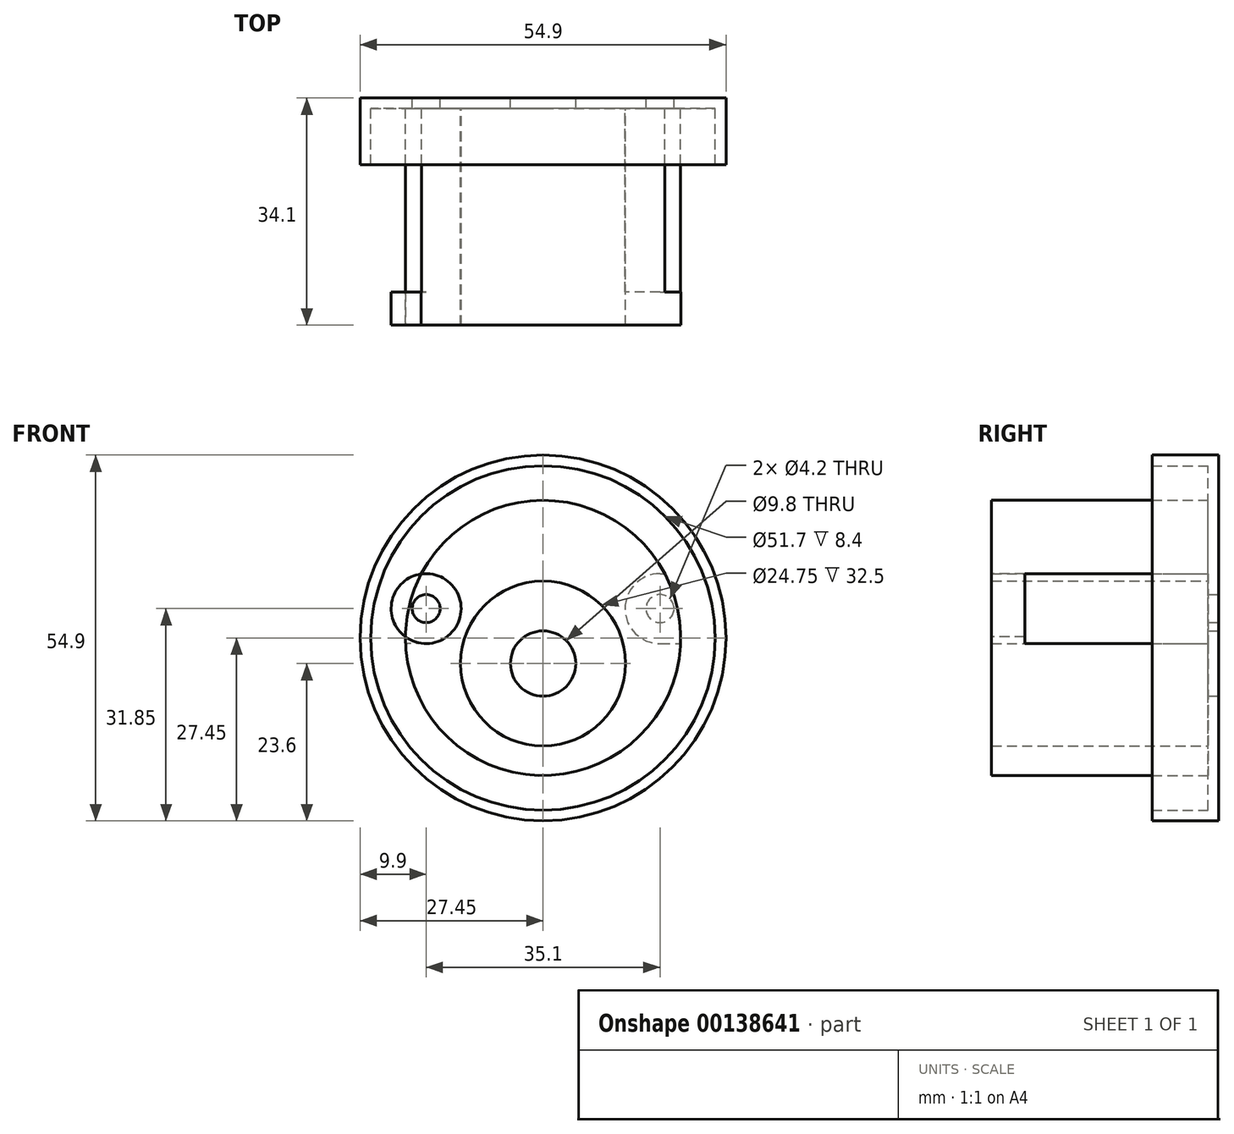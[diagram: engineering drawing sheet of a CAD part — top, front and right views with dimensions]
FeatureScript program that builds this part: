
annotation { "Feature Type Name" : "Feature", "Feature Type Description" : "" }
export const myFeature = defineFeature(function(context is Context, id is Id, definition is map)
    precondition{}
    {
        {
            var Q0;
            Q0=qCreatedBy(makeId("Front.planeOp"),FACE);
            var sketch = newSketch(context, id + "F0", { "sketchPlane" : qUnion([Q0])});
            skCircle(sketch, "E0", {"center": v(0, 0) * mm, "radius": 25.85 * mm});
            skCircle(sketch, "E1.0", {"center": v(0, 0) * mm, "radius": 27.45 * mm});
            skCircle(sketch, "E2", {"center": v(0, -3.85) * mm, "radius": 4.9 * mm});
            skCircle(sketch, "E3", {"center": v(-17.55, 4.4) * mm, "radius": 2.1 * mm});
            skCircle(sketch, "E4", {"center": v(17.55, 4.4) * mm, "radius": 2.1 * mm});
            skLineSegment(sketch, "E5", {"start": v(-17.55, 2.3) * mm, "end": v(17.55, 2.3) * mm, "construction": true});
            skPoint(sketch, "E6", {"position": v(0, 2.3) * mm});
            skCircle(sketch, "E7", {"center": v(0, -3.85) * mm, "radius": 12 * mm, "construction": true});
            skSolve(sketch);
        }
        {
            var Q0;
            Q0=makeQuery(id+"F0.imprint","IMPRINT",FACE,{"disambiguationData":[TD([[makeQuery(id+"F0.imprint","IMPRINT",EDGE,{"derivedFrom":sQuery(id+"F0.wireOp",EDGE,"E0")}),1.0]])]});
            var Q1;
            Q1=makeQuery(id+"F0.imprint","IMPRINT",FACE,{"disambiguationData":[TD([[makeQuery(id+"F0.imprint","IMPRINT",EDGE,{"derivedFrom":sQuery(id+"F0.wireOp",EDGE,"E3")}),-1.0]])]});
            var Q2;
            Q2=makeQuery(id+"F0.imprint","IMPRINT",FACE,{"disambiguationData":[TD([[makeQuery(id+"F0.imprint","IMPRINT",EDGE,{"derivedFrom":sQuery(id+"F0.wireOp",EDGE,"E2")}),-1.0]])]});
            extrude(context, id + "F1", {"entities" : qUnion([Q0, Q1, Q2]), "depth" : 1.6 * mm});
        }
        {
            var Q0;
            Q0=makeQuery(id+"F0.imprint","IMPRINT",FACE,{"disambiguationData":[TD([[makeQuery(id+"F0.imprint","IMPRINT",EDGE,{"derivedFrom":sQuery(id+"F0.wireOp",EDGE,"E0")}),-1.0]])]});
            extrude(context, id + "F2", {"entities" : qUnion([Q0]), "operationType" : NewBodyOperationType.ADD, "depth" : 10 * mm});
        }
        {
            var Q0;
            Q0=makeQuery(id+"F1.opExtrude","CAP_FACE",FACE,{"disambiguationData":[OSD([sQuery(id+"F0.wireOp",EDGE,"E0"),sQuery(id+"F0.wireOp",EDGE,"E2"),sQuery(id+"F0.wireOp",EDGE,"E3"),sQuery(id+"F0.wireOp",EDGE,"E4"),sQuery(id+"F0.wireOp",EDGE,"PUMCyOhg-vD6y-72TI-7Vvg-jFPLf84NLlKd"),sQuery(id+"F0.wireOp",EDGE,"dd9b8376-963c-4b41-b7ff-f7739df00472.0")])],"isStart":false});
            var sketch = newSketch(context, id + "F3", { "sketchPlane" : qUnion([Q0])});
            skCircle(sketch, "E8", {"center": v(0, -3.85) * mm, "radius": 12.38 * mm});
            skCircle(sketch, "E9.0", {"center": v(0, 0) * mm, "radius": 20.65 * mm});
            skCircle(sketch, "E10", {"center": v(-17.55, 4.4) * mm, "radius": 5.25 * mm});
            skCircle(sketch, "E11", {"center": v(17.55, 4.4) * mm, "radius": 5.25 * mm});
            skLineSegment(sketch, "E12", {"start": v(-17.55, 9.65) * mm, "end": v(-18.26, 9.65) * mm});
            skLineSegment(sketch, "E13", {"start": v(-17.55, -0.85) * mm, "end": v(-20.63, -0.85) * mm});
            skLineSegment(sketch, "E14", {"start": v(17.55, 9.65) * mm, "end": v(18.26, 9.65) * mm});
            skLineSegment(sketch, "E15", {"start": v(17.55, -0.85) * mm, "end": v(20.63, -0.85) * mm});
            skSolve(sketch);
        }
        {
            var Q0;
            {var subQ1=sQuery(id+"F3.wireOp",EDGE,"E9.0");var subQ5=sQuery(id+"F3.wireOp",EDGE,"E8");var subQ8=makeQuery(id+"F3.imprint","INTERSECT",VERTEX,{"disambiguationData":[OD(0.0)],"derivedFrom":[subQ5,subQ1]});Q0=makeQuery(id+"F3.imprint","IMPRINT",FACE,{"disambiguationData":[TD([[makeQuery(id+"F3.imprint","IMPRINT",EDGE,{"disambiguationData":[TD([[subQ8,-1.0]])],"derivedFrom":subQ5}),-1.0]])]});}
            extrude(context, id + "F4", {"entities" : qUnion([Q0]), "operationType" : NewBodyOperationType.ADD, "depth" : 32.5 * mm});
        }
        {
            var Q0;
            Q0=makeQuery(id+"F4.opExtrude","CAP_FACE",FACE,{"disambiguationData":[OSD([sQuery(id+"F3.wireOp",EDGE,"E8"),sQuery(id+"F3.wireOp",EDGE,"E9.0"),sQuery(id+"F3.wireOp",EDGE,"E10"),sQuery(id+"F3.wireOp",EDGE,"E11")])],"isStart":false});
            var sketch = newSketch(context, id + "F5", { "sketchPlane" : qUnion([Q0])});
            skCircle(sketch, "E16", {"center": v(-17.55, 4.4) * mm, "radius": 5.25 * mm});
            skCircle(sketch, "E17", {"center": v(17.55, 4.4) * mm, "radius": 5.25 * mm});
            skCircle(sketch, "E18", {"center": v(0, 0) * mm, "radius": 20.65 * mm});
            skLineSegment(sketch, "E19", {"start": v(-17.55, -0.85) * mm, "end": v(-20.63, -0.85) * mm});
            skLineSegment(sketch, "E20", {"start": v(-20.63, -0.85) * mm, "end": v(-20.67, 0.18) * mm});
            skLineSegment(sketch, "E21", {"start": v(-17.55, 9.65) * mm, "end": v(-18.26, 9.65) * mm});
            skLineSegment(sketch, "E22", {"start": v(-18.26, 9.65) * mm, "end": v(-18.28, 9.6) * mm});
            skLineSegment(sketch, "E23", {"start": v(17.55, 9.65) * mm, "end": v(18.26, 9.65) * mm});
            skLineSegment(sketch, "E24", {"start": v(18.26, 9.65) * mm, "end": v(18.28, 9.6) * mm});
            skLineSegment(sketch, "E25", {"start": v(17.55, -0.85) * mm, "end": v(20.63, -0.85) * mm});
            skLineSegment(sketch, "E26", {"start": v(20.63, -0.85) * mm, "end": v(20.67, 0.18) * mm});
            skSolve(sketch);
        }
        {
            var Q0;
            {var subQ0=sQuery(id+"F5.wireOp",EDGE,"E18");var subQ1=sQuery(id+"F5.wireOp",EDGE,"E16");var subQ2=makeQuery(id+"F5.imprint","INTERSECT",VERTEX,{"disambiguationData":[OD(0.0)],"derivedFrom":[subQ1,subQ0]});Q0=makeQuery(id+"F5.imprint","IMPRINT",FACE,{"disambiguationData":[TD([[makeQuery(id+"F5.imprint","IMPRINT",EDGE,{"disambiguationData":[TD([[subQ2,1.0]])],"derivedFrom":subQ1}),1.0]])]});}
            var Q1;
            {var subQ0=sQuery(id+"F5.wireOp",EDGE,"E21");Q1=makeQuery(id+"F5.imprint","IMPRINT",FACE,{"disambiguationData":[TD([[makeQuery(id+"F5.imprint","IMPRINT",EDGE,{"derivedFrom":subQ0}),1.0]])]});}
            var Q2;
            {var subQ0=sQuery(id+"F5.wireOp",EDGE,"E19");Q2=makeQuery(id+"F5.imprint","IMPRINT",FACE,{"disambiguationData":[TD([[makeQuery(id+"F5.imprint","IMPRINT",EDGE,{"derivedFrom":subQ0}),-1.0]])]});}
            var Q3;
            {var subQ0=sQuery(id+"F5.wireOp",EDGE,"E17");var subQ1=makeQuery(id+"F5.imprint","INTERSECT",VERTEX,{"derivedFrom":[subQ0,sQuery(id+"F5.wireOp",EDGE,"E23")]});Q3=makeQuery(id+"F5.imprint","IMPRINT",FACE,{"disambiguationData":[TD([[makeQuery(id+"F5.imprint","IMPRINT",EDGE,{"disambiguationData":[TD([[subQ1,1.0]])],"derivedFrom":subQ0}),1.0]])]});}
            var Q4;
            {var subQ0=sQuery(id+"F5.wireOp",EDGE,"E25");Q4=makeQuery(id+"F5.imprint","IMPRINT",FACE,{"disambiguationData":[TD([[makeQuery(id+"F5.imprint","IMPRINT",EDGE,{"derivedFrom":subQ0}),1.0]])]});}
            var Q5;
            {var subQ0=sQuery(id+"F5.wireOp",EDGE,"E23");Q5=makeQuery(id+"F5.imprint","IMPRINT",FACE,{"disambiguationData":[TD([[makeQuery(id+"F5.imprint","IMPRINT",EDGE,{"derivedFrom":subQ0}),-1.0]])]});}
            extrude(context, id + "F6", {"entities" : qUnion([Q0, Q1, Q2, Q3, Q4, Q5]), "operationType" : NewBodyOperationType.ADD, "oppositeDirection" : true, "depth" : 5 * mm});
        }
    });
